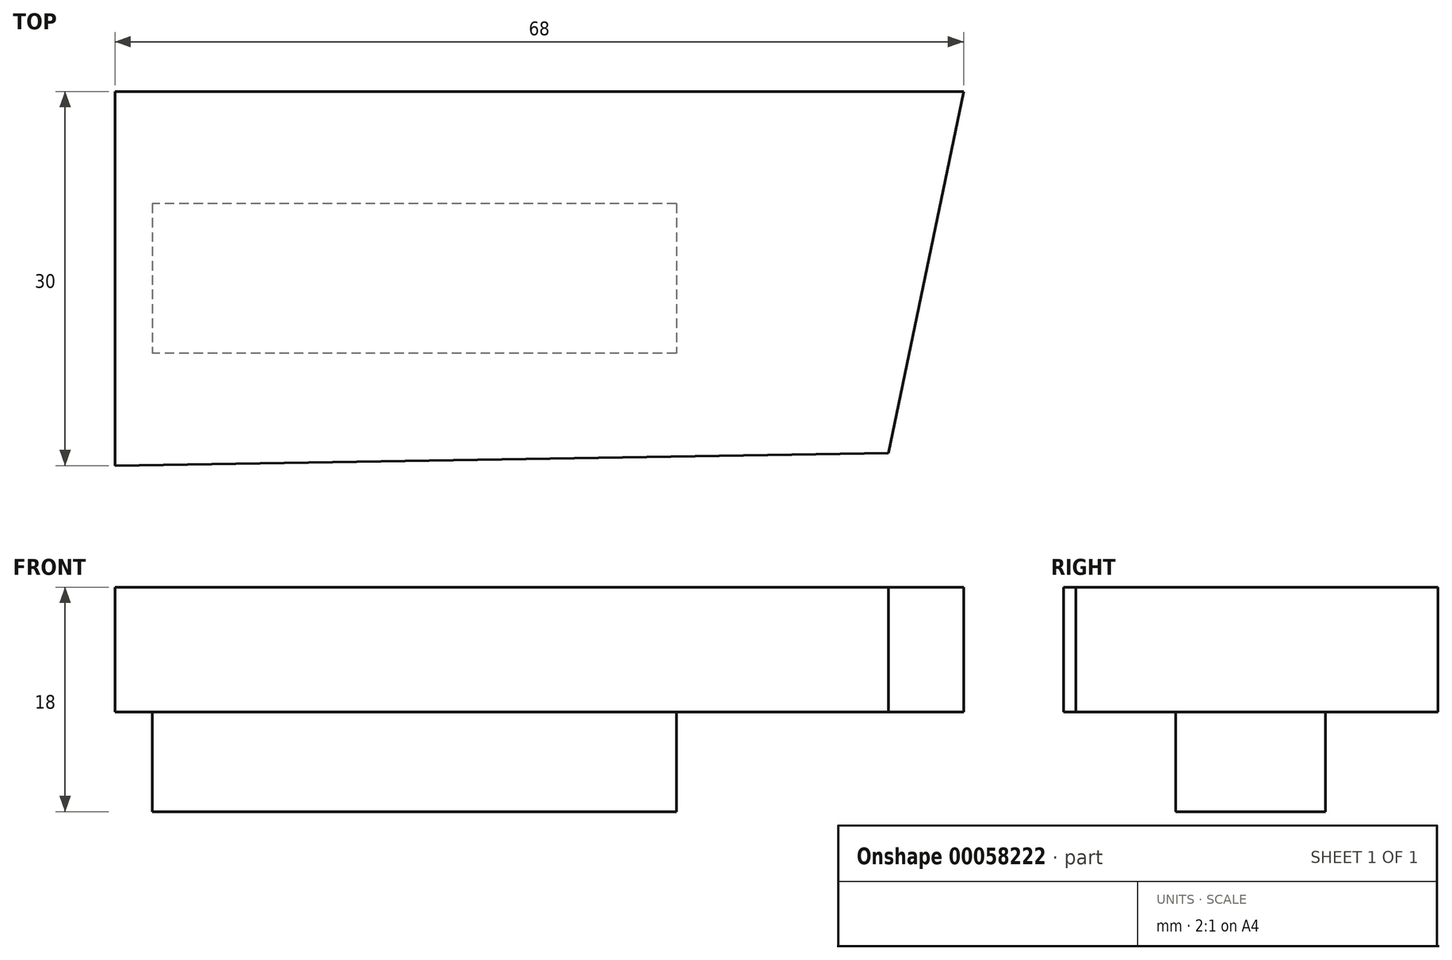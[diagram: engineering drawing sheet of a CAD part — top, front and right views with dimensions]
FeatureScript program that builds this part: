
annotation { "Feature Type Name" : "Feature", "Feature Type Description" : "" }
export const myFeature = defineFeature(function(context is Context, id is Id, definition is map)
    precondition{}
    {
        {
            var Q0;
            Q0=qCreatedBy(makeId("Top.planeOp"),FACE);
            var sketch = newSketch(context, id + "F0", { "sketchPlane" : qUnion([Q0])});
            skPoint(sketch, "E0.rect.middle", {"position": v(0, 0) * mm});
            skLineSegment(sketch, "E1", {"start": v(-41.62, 18.43) * mm, "end": v(26.38, 18.43) * mm});
            skLineSegment(sketch, "E2", {"start": v(26.38, 18.43) * mm, "end": v(20.37, -10.57) * mm});
            skLineSegment(sketch, "E3", {"start": v(20.37, -10.57) * mm, "end": v(-41.62, -11.57) * mm});
            skLineSegment(sketch, "E4", {"start": v(-41.62, -11.57) * mm, "end": v(-41.62, 18.43) * mm});
            skLineSegment(sketch, "E5", {"start": v(20.37, -10.57) * mm, "end": v(20.37, 18.43) * mm, "construction": true});
            skSolve(sketch);
        }
        {
            var Q0;
            Q0 = qSketchRegion(id + "F0", true);
            extrude(context, id + "F1", {"entities" : qUnion([Q0]), "depth" : 10 * mm});
        }
        {
            var Q0;
            Q0=makeQuery(id+"F1.opExtrude","CAP_FACE",FACE,{"disambiguationData":[OSD([sQuery(id+"F0.wireOp",EDGE,"E1"),sQuery(id+"F0.wireOp",EDGE,"E2"),sQuery(id+"F0.wireOp",EDGE,"E3"),sQuery(id+"F0.wireOp",EDGE,"E4")])],"isStart":true});
            var sketch = newSketch(context, id + "F2", { "sketchPlane" : qUnion([Q0])});
            skLineSegment(sketch, "E6.rect.bottom", {"start": v(3.38, -9.43) * mm, "end": v(-38.62, -9.43) * mm});
            skLineSegment(sketch, "E6.rect.top", {"start": v(3.38, 2.57) * mm, "end": v(-38.62, 2.57) * mm});
            skLineSegment(sketch, "E6.rect.left", {"start": v(3.38, -9.43) * mm, "end": v(3.38, 2.57) * mm});
            skLineSegment(sketch, "E6.rect.right", {"start": v(-38.62, -9.43) * mm, "end": v(-38.62, 2.57) * mm});
            skPoint(sketch, "E6.rect.middle", {"position": v(-17.62, -3.43) * mm});
            skPoint(sketch, "E7", {"position": v(-41.62, -3.43) * mm});
            skLineSegment(sketch, "E8", {"start": v(-41.62, -7.7) * mm, "end": v(-38.62, -7.7) * mm, "construction": true});
            skSolve(sketch);
        }
        {
            var Q0;
            Q0 = qSketchRegion(id + "F2", true);
            extrude(context, id + "F3", {"entities" : qUnion([Q0]), "operationType" : NewBodyOperationType.ADD, "depth" : 8 * mm});
        }
    });
